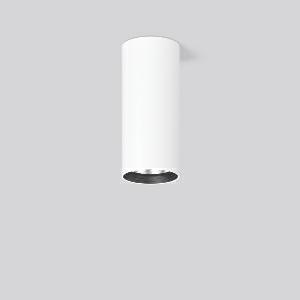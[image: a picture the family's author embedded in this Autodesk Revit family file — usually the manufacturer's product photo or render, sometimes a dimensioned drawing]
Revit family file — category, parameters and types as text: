
# Revit family: heledon_mini_a_931210_002_76_2db4
name_source: partatom
category: Lighting Fixtures
units: mm (PartAtom-declared; Revit-internal decimal feet)

## family parameters
Cut with Voids When Loaded = No
Host = Face
Light Source = No
Part Type = Normal
Room Calculation Point = No
Round Connector Dimension = Use Diameter
Shared = No

## types (1)
- HELEDON mini A (1 x LED Modul 930, 3650 lm, 3000)
    Apparent Load = 29 VA
    Approval mark = CE
    CIE Flux Codes = 95 99 100 100 100
    Color Rendering = 90
    Color Temperature = 3000
    Default Elevation = 1800 mm
    Description = Series: HELEDON mini
Cylindrical surface-mounted downlight. Housing: die-cast aluminium, powder-coated. Internal ceiling frame polycarbonate with bayonet mounting. Black plastic ring and recessed LED to prevent glare from the side. Optical assembly with reflector made of MIRO-Silver with 98% total light reflection for outstanding efficiency - can be changed without tools. Best colour rendering index Ra>90. Suitable for Ceiling mounting. Easy installation with a separate ceiling frame with bayonet mounting and plug connection. Driver integrated. Connected via plug-in connector. High quality converter without flickering and stroboscopic effect. The following accessories can be mounted without use of tools: interchangeable lenses, decorative glasses, honeycomb louvre, clear and frosted diffusers, white interchangeable plastic ring. 
Colour: traffic white, matt (RAL 9016)
Diameter: 87 mm
Height: 197 mm
Lamp: LED
Socket: without socket
Colour temperature: 3000K
Colour rendering index (CRI): 92
System power: 29 W
Rated luminous flux: 3650 lm
Luminous efficiency: 126 lm/W
Control gear: Converter, dimmable, DALI
Protection class: I
Type of protection: IP 20
    Height = 197 mm
    Lamp = 1 x LED Modul 930
    Lamp Light Flux = 3650 lm
    Lamp count = 1
    Length = 87 mm
    Lifetime = 50000 h
    Luminous efficacy = 126 lm/W
    Manufacturer = RZB
    ModVariant = No
    Model = 931210.002.76
    Mounting Place = Ceiling
    Mounting Type = Surface mounted
    Number of Poles = 1
    OnlyDefault = Yes
    Power Factor = 1
    Product Name = HELEDON mini A
    Product group = Surface mounted downlights
    ProductGroupID = 302
    Protection Class = Protection class I
    Protection Degree = IP 20
    RLX_Detail_Level = 1
    RLX_Emergency_Light_Flux = 0 lm
    RLX_Emergency_Type = 0
    RLX_Emergency_Type_DB = No
    RlxData = <blob elided: 108265 chars, md5=f2ac8b89>
    Socket = socket
    Standby Power = 0 W
    System Light Flux = 3650 lm
    System Power = 29 W
    Type Comments = Product without accessories
    Type Image = 931188.002.jpg
    URL = http://relux.com
    VarID = ---
    Voltage = 230 V
    Voltage Range = 220-240 V
    Weight = 0.00 kg
    Width = 0 mm  [stored 0 ft]

note: [stored X ft] marks values corroborated as IEEE doubles in the binary element streams (Revit-internal decimal feet)

## geometry (parser evidence)
native form markers: Blend x4, Sweep x10
no freeform markers — native parametric forms only
